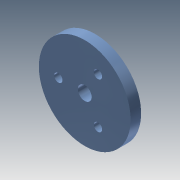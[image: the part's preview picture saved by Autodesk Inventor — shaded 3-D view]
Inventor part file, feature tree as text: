
AUTODESK INVENTOR PART (.ipt)
format: ipt  version: 2013 (Build 170138000, 138)  size: 95,232 bytes
history: native  units: mm
features: extrude x2, sketch x2
ambient origin geometry x8: Origin, YZ Plane, XZ Plane, XY Plane, X Axis, Y Axis, Z Axis, Center Point
bodies: Solid1 (feature_tree)
feature tree (4):
  extrude  "Extrusion1"  Depth=5.0mm
  extrude  "Extrusion2"  Depth=3.0mm
  sketch  "Sketch1"  dims[d0=33.15mm d1=5.0mm]
  sketch  "Sketch2"  dims[d2=3.8mm d3=0.0mm d4=3.0mm d7=3.0mm d8=3.0mm d9=3.8mm d10=0.0mm]
